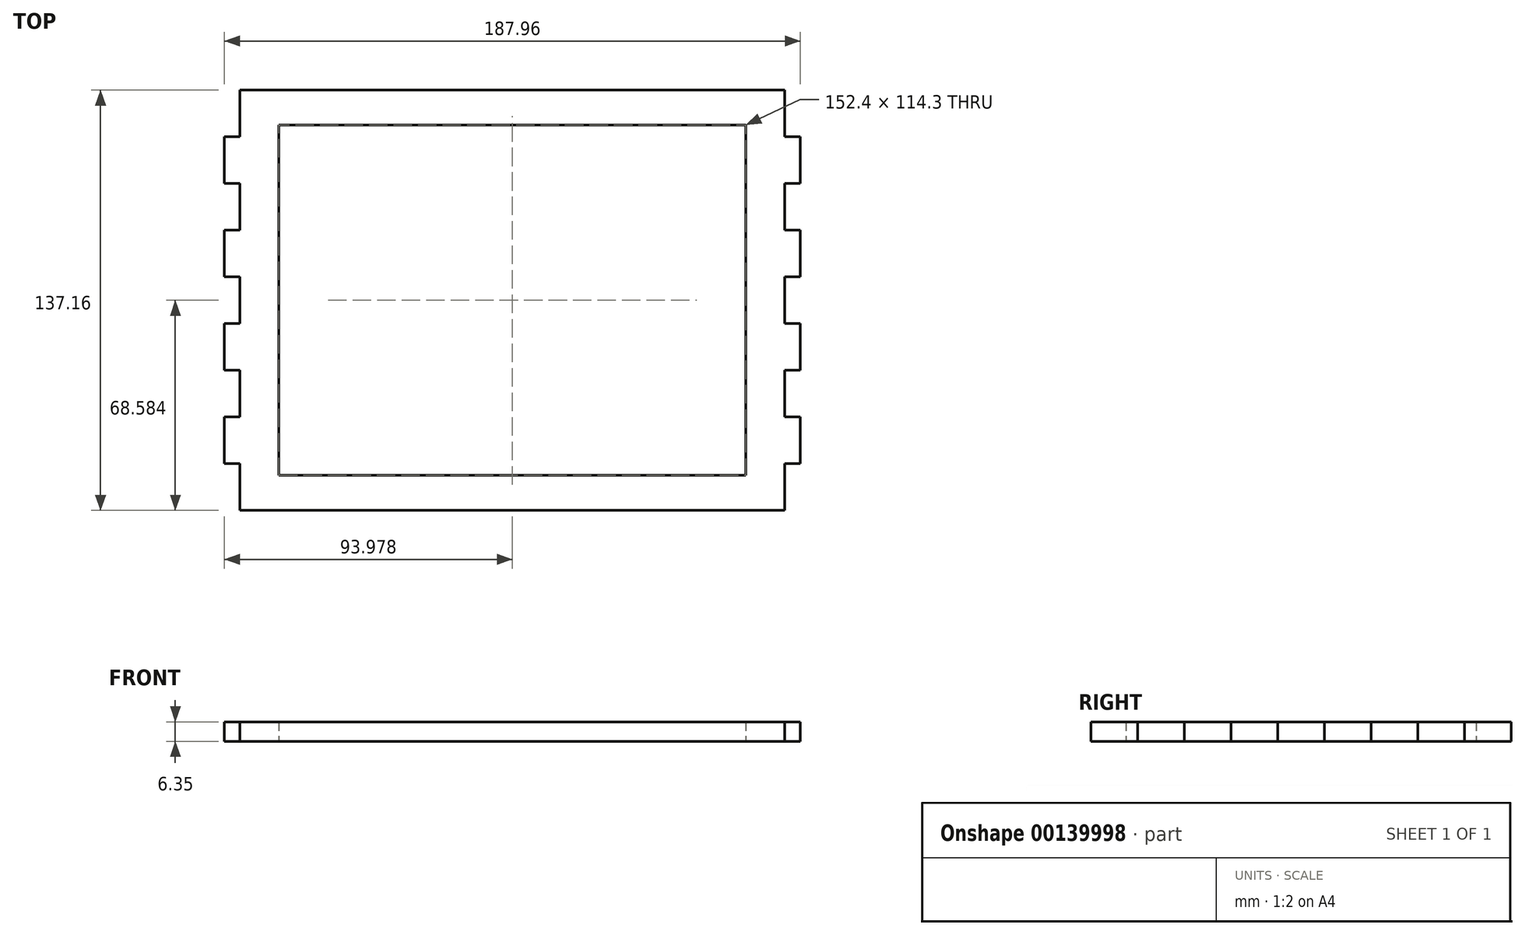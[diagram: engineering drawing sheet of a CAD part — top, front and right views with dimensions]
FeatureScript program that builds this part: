
annotation { "Feature Type Name" : "Feature", "Feature Type Description" : "" }
export const myFeature = defineFeature(function(context is Context, id is Id, definition is map)
    precondition{}
    {
        {
            var Q0;
            Q0=qCreatedBy(makeId("Top.planeOp"),FACE);
            var sketch = newSketch(context, id + "F0", { "sketchPlane" : qUnion([Q0])});
            skLineSegment(sketch, "E0", {"start": v(89.06, 68.85) * mm, "end": v(89.06, 53.61) * mm});
            skLineSegment(sketch, "E1", {"start": v(89.06, 53.61) * mm, "end": v(94.14, 53.61) * mm});
            skLineSegment(sketch, "E2", {"start": v(94.14, 53.61) * mm, "end": v(94.14, 38.37) * mm});
            skLineSegment(sketch, "E3", {"start": v(94.14, 38.37) * mm, "end": v(89.06, 38.37) * mm});
            skLineSegment(sketch, "E4", {"start": v(89.06, 38.37) * mm, "end": v(89.06, 23.13) * mm});
            skLineSegment(sketch, "E5", {"start": v(89.06, 23.13) * mm, "end": v(94.14, 23.13) * mm});
            skLineSegment(sketch, "E6", {"start": v(94.14, 23.13) * mm, "end": v(94.14, 7.9) * mm});
            skLineSegment(sketch, "E7", {"start": v(94.14, 7.9) * mm, "end": v(89.06, 7.9) * mm});
            skLineSegment(sketch, "E8", {"start": v(89.06, 7.9) * mm, "end": v(89.06, -7.35) * mm});
            skLineSegment(sketch, "E9", {"start": v(89.06, -7.35) * mm, "end": v(94.14, -7.35) * mm});
            skLineSegment(sketch, "E10", {"start": v(94.14, -7.35) * mm, "end": v(94.14, -22.59) * mm});
            skLineSegment(sketch, "E11", {"start": v(94.14, -22.59) * mm, "end": v(89.06, -22.59) * mm});
            skLineSegment(sketch, "E12", {"start": v(89.06, -22.59) * mm, "end": v(89.06, -37.83) * mm});
            skLineSegment(sketch, "E13", {"start": v(89.06, -37.83) * mm, "end": v(94.14, -37.83) * mm});
            skLineSegment(sketch, "E14", {"start": v(94.14, -37.83) * mm, "end": v(94.14, -53.07) * mm});
            skLineSegment(sketch, "E15", {"start": v(94.14, -53.07) * mm, "end": v(89.06, -53.07) * mm});
            skLineSegment(sketch, "E16", {"start": v(89.06, -53.07) * mm, "end": v(89.06, -68.3) * mm});
            skLineSegment(sketch, "E17", {"start": v(-88.74, 68.85) * mm, "end": v(-88.74, 53.61) * mm});
            skLineSegment(sketch, "E18", {"start": v(-88.74, 53.61) * mm, "end": v(-93.82, 53.61) * mm});
            skLineSegment(sketch, "E19", {"start": v(-93.82, 53.61) * mm, "end": v(-93.82, 38.37) * mm});
            skLineSegment(sketch, "E20", {"start": v(-93.82, 38.37) * mm, "end": v(-88.74, 38.37) * mm});
            skLineSegment(sketch, "E21", {"start": v(-88.74, 38.37) * mm, "end": v(-88.74, 23.13) * mm});
            skLineSegment(sketch, "E22", {"start": v(-88.74, 23.13) * mm, "end": v(-93.82, 23.13) * mm});
            skLineSegment(sketch, "E23", {"start": v(-93.82, 23.13) * mm, "end": v(-93.82, 7.9) * mm});
            skLineSegment(sketch, "E24", {"start": v(-93.82, 7.9) * mm, "end": v(-88.74, 7.9) * mm});
            skLineSegment(sketch, "E25", {"start": v(-88.74, 7.9) * mm, "end": v(-88.74, -7.35) * mm});
            skLineSegment(sketch, "E26", {"start": v(-88.74, -7.35) * mm, "end": v(-93.82, -7.35) * mm});
            skLineSegment(sketch, "E27", {"start": v(-93.82, -7.35) * mm, "end": v(-93.82, -22.59) * mm});
            skLineSegment(sketch, "E28", {"start": v(-93.82, -22.59) * mm, "end": v(-88.74, -22.59) * mm});
            skLineSegment(sketch, "E29", {"start": v(-88.74, -22.59) * mm, "end": v(-88.74, -37.83) * mm});
            skLineSegment(sketch, "E30", {"start": v(-88.74, -37.83) * mm, "end": v(-93.82, -37.83) * mm});
            skLineSegment(sketch, "E31", {"start": v(-93.82, -37.83) * mm, "end": v(-93.82, -53.07) * mm});
            skLineSegment(sketch, "E32", {"start": v(-93.82, -53.07) * mm, "end": v(-88.74, -53.07) * mm});
            skLineSegment(sketch, "E33", {"start": v(-88.74, -53.07) * mm, "end": v(-88.74, -68.3) * mm});
            skLineSegment(sketch, "E34", {"start": v(-85.01, -3.29) * mm, "end": v(72.99, -3.29) * mm, "construction": true});
            skLineSegment(sketch, "E35", {"start": v(-88.74, 68.85) * mm, "end": v(89.06, 68.85) * mm});
            skLineSegment(sketch, "E36", {"start": v(-88.74, -68.3) * mm, "end": v(89.06, -68.3) * mm});
            skLineSegment(sketch, "E37.bottom", {"start": v(-76.04, 57.42) * mm, "end": v(76.36, 57.42) * mm});
            skLineSegment(sketch, "E37.top", {"start": v(-76.04, -56.88) * mm, "end": v(76.36, -56.88) * mm});
            skLineSegment(sketch, "E37.left", {"start": v(-76.04, 57.42) * mm, "end": v(-76.04, -56.88) * mm});
            skLineSegment(sketch, "E37.right", {"start": v(76.36, 57.42) * mm, "end": v(76.36, -56.88) * mm});
            skSolve(sketch);
        }
        {
            var Q0;
            Q0=makeQuery(id+"F0.imprint","IMPRINT",FACE,{"disambiguationData":[TD([[makeQuery(id+"F0.imprint","IMPRINT",EDGE,{"derivedFrom":sQuery(id+"F0.wireOp",EDGE,"E0")}),-1.0]])]});
            extrude(context, id + "F1", {"entities" : qUnion([Q0]), "depth" : 6.35 * mm});
        }
    });
